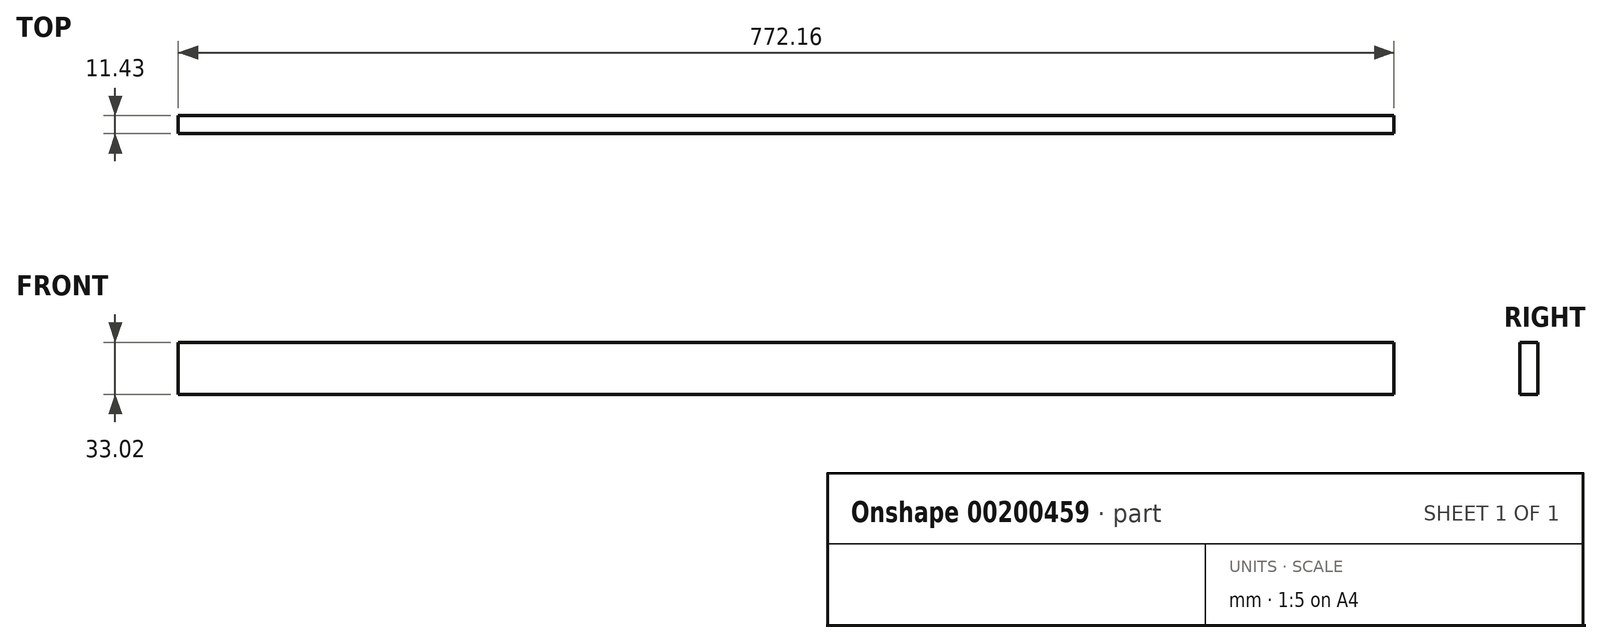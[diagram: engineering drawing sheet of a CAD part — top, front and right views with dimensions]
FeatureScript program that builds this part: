
annotation { "Feature Type Name" : "Feature", "Feature Type Description" : "" }
export const myFeature = defineFeature(function(context is Context, id is Id, definition is map)
    precondition{}
    {
        {
            var Q0;
            Q0=qCreatedBy(makeId("Front.planeOp"),FACE);
            var sketch = newSketch(context, id + "F0", { "sketchPlane" : qUnion([Q0])});
            skLineSegment(sketch, "E0.bottom", {"start": v(-930.12, 33.02) * mm, "end": v(-157.96, 33.02) * mm});
            skLineSegment(sketch, "E0.top", {"start": v(-930.12, 0) * mm, "end": v(-157.96, 0) * mm});
            skLineSegment(sketch, "E0.left", {"start": v(-930.12, 33.02) * mm, "end": v(-930.12, 0) * mm});
            skLineSegment(sketch, "E0.right", {"start": v(-157.96, 33.02) * mm, "end": v(-157.96, 0) * mm});
            skSolve(sketch);
        }
        {
            var Q0;
            Q0 = qSketchRegion(id + "F0", true);
            extrude(context, id + "F1", {"entities" : qUnion([Q0]), "depth" : 11.43 * mm});
        }
    });
